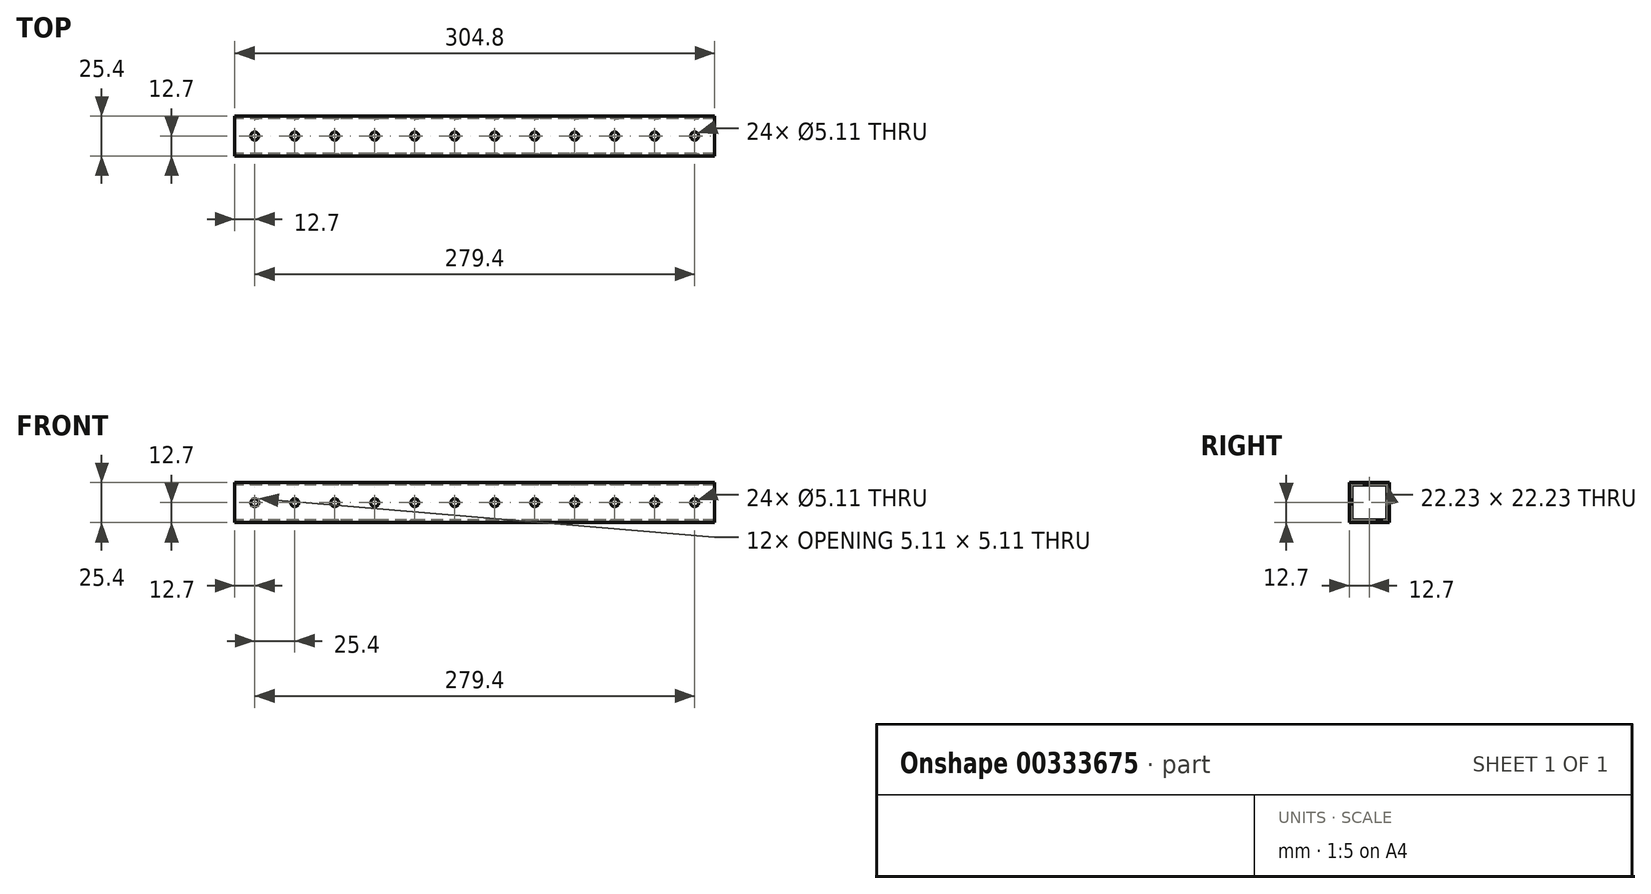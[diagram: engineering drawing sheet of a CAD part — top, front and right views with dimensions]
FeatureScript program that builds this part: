
annotation { "Feature Type Name" : "Feature", "Feature Type Description" : "" }
export const myFeature = defineFeature(function(context is Context, id is Id, definition is map)
    precondition{}
    {
        {
            var Q0;
            Q0=qCreatedBy(makeId("Right.planeOp"),FACE);
            var sketch = newSketch(context, id + "F0", { "sketchPlane" : qUnion([Q0])});
            skLineSegment(sketch, "E0.bottom", {"start": v(12.7, 12.7) * mm, "end": v(-12.7, 12.7) * mm});
            skLineSegment(sketch, "E0.top", {"start": v(12.7, -12.7) * mm, "end": v(-12.7, -12.7) * mm});
            skLineSegment(sketch, "E0.left", {"start": v(12.7, 12.7) * mm, "end": v(12.7, -12.7) * mm});
            skLineSegment(sketch, "E0.right", {"start": v(-12.7, 12.7) * mm, "end": v(-12.7, -12.7) * mm});
            skPoint(sketch, "E0.middle", {"position": v(0, 0) * mm});
            skSolve(sketch);
        }
        {
            var Q0;
            Q0=makeQuery(id+"F0.imprint","IMPRINT",FACE,{"disambiguationData":[TD([[makeQuery(id+"F0.imprint","IMPRINT",EDGE,{"derivedFrom":sQuery(id+"F0.wireOp",EDGE,"E0.bottom")}),1.0]])]});
            extrude(context, id + "F1", {"entities" : qUnion([Q0]), "depth" : 304.8 * mm});
        }
        {
            var Q0;
            Q0=makeQuery(id+"F1.opExtrude","SWEPT_FACE",FACE,{"disambiguationData":[OSD([sQuery(id+"F0.wireOp",EDGE,"E0.right")])]});
            var sketch = newSketch(context, id + "F2", { "sketchPlane" : qUnion([Q0])});
            skCircle(sketch, "E1", {"center": v(12.7, 0) * mm, "radius": 2.55 * mm});
            skCircle(sketch, "E2.1.0.0", {"center": v(38.1, 0) * mm, "radius": 2.55 * mm});
            skCircle(sketch, "E2.2.0.0", {"center": v(63.5, 0) * mm, "radius": 2.55 * mm});
            skCircle(sketch, "E2.3.0.0", {"center": v(88.9, 0) * mm, "radius": 2.55 * mm});
            skCircle(sketch, "E2.4.0.0", {"center": v(114.3, 0) * mm, "radius": 2.55 * mm});
            skCircle(sketch, "E2.5.0.0", {"center": v(139.7, 0) * mm, "radius": 2.55 * mm});
            skCircle(sketch, "E2.6.0.0", {"center": v(165.1, 0) * mm, "radius": 2.55 * mm});
            skCircle(sketch, "E2.7.0.0", {"center": v(190.5, 0) * mm, "radius": 2.55 * mm});
            skCircle(sketch, "E2.8.0.0", {"center": v(215.9, 0) * mm, "radius": 2.55 * mm});
            skCircle(sketch, "E2.9.0.0", {"center": v(241.3, 0) * mm, "radius": 2.55 * mm});
            skCircle(sketch, "E2.10.0.0", {"center": v(266.7, 0) * mm, "radius": 2.55 * mm});
            skCircle(sketch, "E2.11.0.0", {"center": v(292.1, 0) * mm, "radius": 2.55 * mm});
            skLineSegment(sketch, "E2.direction1", {"start": v(12.7, 0) * mm, "end": v(38.1, 0) * mm, "construction": true});
            skSolve(sketch);
        }
        {
            var Q0;
            Q0=qSketchRegion(id+"F2",true);
            extrude(context, id + "F3", {"entities" : qUnion([Q0]), "operationType" : NewBodyOperationType.REMOVE, "oppositeDirection" : true, "depth" : 25.4 * mm});
        }
        {
            var Q0;
            Q0=makeQuery(id+"F1.opExtrude","CAP_FACE",FACE,{"disambiguationData":[OSD([sQuery(id+"F0.wireOp",EDGE,"E0.bottom"),sQuery(id+"F0.wireOp",EDGE,"E0.top"),sQuery(id+"F0.wireOp",EDGE,"E0.left"),sQuery(id+"F0.wireOp",EDGE,"E0.right")])],"isStart":true});
            var sketch = newSketch(context, id + "F4", { "sketchPlane" : qUnion([Q0])});
            skLineSegment(sketch, "E3.bottom", {"start": v(11.11, 11.11) * mm, "end": v(-11.11, 11.11) * mm});
            skLineSegment(sketch, "E3.top", {"start": v(11.11, -11.11) * mm, "end": v(-11.11, -11.11) * mm});
            skLineSegment(sketch, "E3.left", {"start": v(11.11, 11.11) * mm, "end": v(11.11, -11.11) * mm});
            skLineSegment(sketch, "E3.right", {"start": v(-11.11, 11.11) * mm, "end": v(-11.11, -11.11) * mm});
            skPoint(sketch, "E3.middle", {"position": v(0, 0) * mm});
            skSolve(sketch);
        }
        {
            var Q0;
            Q0=makeQuery(id+"F4.imprint","IMPRINT",FACE,{"disambiguationData":[TD([[makeQuery(id+"F4.imprint","IMPRINT",EDGE,{"derivedFrom":sQuery(id+"F4.wireOp",EDGE,"E3.bottom")}),1.0]])]});
            extrude(context, id + "F5", {"entities" : qUnion([Q0]), "operationType" : NewBodyOperationType.REMOVE, "oppositeDirection" : true, "depth" : 304.8 * mm});
        }
        {
            var Q0;
            Q0=makeQuery(id+"F1.opExtrude","SWEPT_FACE",FACE,{"disambiguationData":[OSD([sQuery(id+"F0.wireOp",EDGE,"E0.bottom")])]});
            var sketch = newSketch(context, id + "F6", { "sketchPlane" : qUnion([Q0])});
            skCircle(sketch, "E4", {"center": v(12.7, 0) * mm, "radius": 2.55 * mm});
            skCircle(sketch, "E5.1.0.0", {"center": v(38.1, 0) * mm, "radius": 2.55 * mm});
            skCircle(sketch, "E5.2.0.0", {"center": v(63.5, 0) * mm, "radius": 2.55 * mm});
            skCircle(sketch, "E5.3.0.0", {"center": v(88.9, 0) * mm, "radius": 2.55 * mm});
            skCircle(sketch, "E5.4.0.0", {"center": v(114.3, 0) * mm, "radius": 2.55 * mm});
            skCircle(sketch, "E5.5.0.0", {"center": v(139.7, 0) * mm, "radius": 2.55 * mm});
            skCircle(sketch, "E5.6.0.0", {"center": v(165.1, 0) * mm, "radius": 2.55 * mm});
            skCircle(sketch, "E5.7.0.0", {"center": v(190.5, 0) * mm, "radius": 2.55 * mm});
            skCircle(sketch, "E5.8.0.0", {"center": v(215.9, 0) * mm, "radius": 2.55 * mm});
            skCircle(sketch, "E5.9.0.0", {"center": v(241.3, 0) * mm, "radius": 2.55 * mm});
            skCircle(sketch, "E5.10.0.0", {"center": v(266.7, 0) * mm, "radius": 2.55 * mm});
            skCircle(sketch, "E5.11.0.0", {"center": v(292.1, 0) * mm, "radius": 2.55 * mm});
            skLineSegment(sketch, "E5.direction1", {"start": v(12.7, 0) * mm, "end": v(38.1, 0) * mm, "construction": true});
            skSolve(sketch);
        }
        {
            var Q0;
            Q0=qSketchRegion(id+"F6",true);
            extrude(context, id + "F7", {"entities" : qUnion([Q0]), "operationType" : NewBodyOperationType.REMOVE, "oppositeDirection" : true, "depth" : 25.4 * mm});
        }
    });
